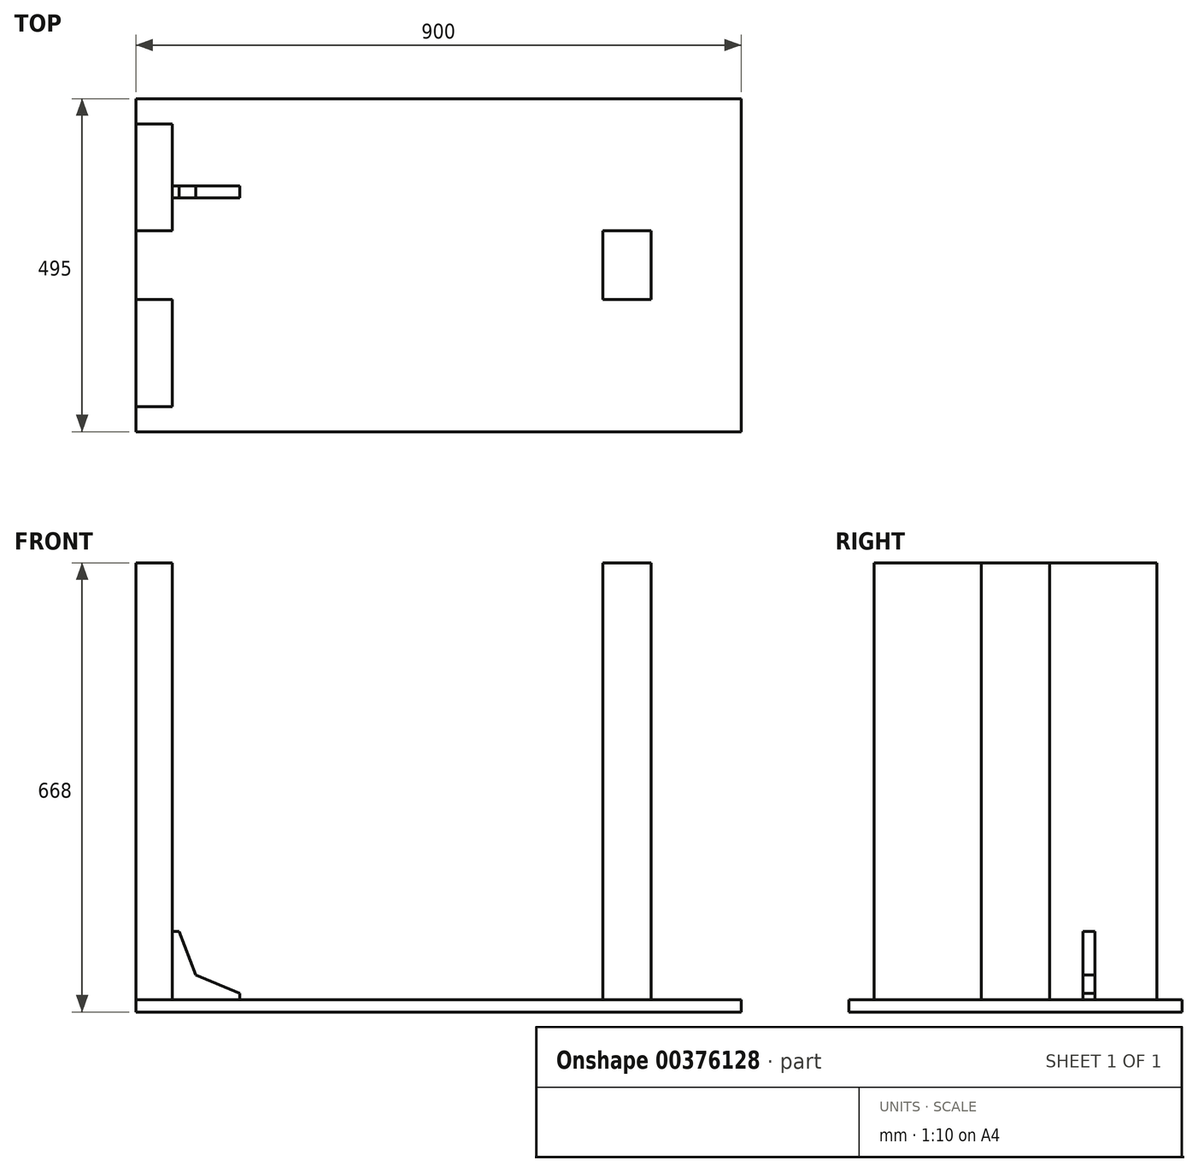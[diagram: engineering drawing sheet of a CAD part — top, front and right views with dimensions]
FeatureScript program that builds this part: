
annotation { "Feature Type Name" : "Feature", "Feature Type Description" : "" }
export const myFeature = defineFeature(function(context is Context, id is Id, definition is map)
    precondition{}
    {
        {
            var Q0;
            Q0=qCreatedBy(makeId("Top.planeOp"),FACE);
            var sketch = newSketch(context, id + "F0", { "sketchPlane" : qUnion([Q0])});
            skLineSegment(sketch, "E0.bottom", {"start": v(-450, 247.5) * mm, "end": v(450, 247.5) * mm});
            skLineSegment(sketch, "E0.top", {"start": v(-450, -247.5) * mm, "end": v(450, -247.5) * mm});
            skLineSegment(sketch, "E0.left", {"start": v(-450, 247.5) * mm, "end": v(-450, -247.5) * mm});
            skLineSegment(sketch, "E0.right", {"start": v(450, 247.5) * mm, "end": v(450, -247.5) * mm});
            skPoint(sketch, "E1", {"position": v(0, 247.5) * mm});
            skPoint(sketch, "E2", {"position": v(-450, 0) * mm});
            skSolve(sketch);
        }
        {
            var Q0;
            Q0=qSketchRegion(id+"F0",true);
            extrude(context, id + "F1", {"entities" : qUnion([Q0]), "depth" : 18 * mm});
        }
        {
            var Q0;
            Q0=makeQuery(id+"F1.opExtrude","CAP_FACE",FACE,{"disambiguationData":[OSD([sQuery(id+"F0.wireOp",EDGE,"E0.bottom"),sQuery(id+"F0.wireOp",EDGE,"E0.top"),sQuery(id+"F0.wireOp",EDGE,"E0.left"),sQuery(id+"F0.wireOp",EDGE,"E0.right")])],"isStart":false});
            var sketch = newSketch(context, id + "F2", { "sketchPlane" : qUnion([Q0])});
            skPoint(sketch, "E3", {"position": v(-450, 0) * mm});
            skLineSegment(sketch, "E4.bottom", {"start": v(-450, 210) * mm, "end": v(-396, 210) * mm});
            skLineSegment(sketch, "E4.top", {"start": v(-450, -210) * mm, "end": v(-396, -210) * mm});
            skLineSegment(sketch, "E4.left", {"start": v(-450, 210) * mm, "end": v(-450, -210) * mm});
            skLineSegment(sketch, "E4.right", {"start": v(-396, 210) * mm, "end": v(-396, -210) * mm});
            skLineSegment(sketch, "E5.bottom", {"start": v(316, -51) * mm, "end": v(244, -51) * mm});
            skLineSegment(sketch, "E5.top", {"start": v(316, 51) * mm, "end": v(244, 51) * mm});
            skLineSegment(sketch, "E5.left", {"start": v(316, -51) * mm, "end": v(316, 51) * mm});
            skLineSegment(sketch, "E5.right", {"start": v(244, -51) * mm, "end": v(244, 51) * mm});
            skPoint(sketch, "E6", {"position": v(316, 0) * mm});
            skPoint(sketch, "E7", {"position": v(0, -247.5) * mm});
            skSolve(sketch);
        }
        {
            var Q0;
            {var subQ1=sQuery(id+"F2.wireOp",EDGE,"E4.bottom");Q0=makeQuery(id+"F2.imprint","IMPRINT",FACE,{"disambiguationData":[TD([[makeQuery(id+"F2.imprint","IMPRINT",EDGE,{"derivedFrom":subQ1}),-1.0]])]});}
            var Q1;
            Q1=makeQuery(id+"F2.imprint","IMPRINT",FACE,{"disambiguationData":[TD([[makeQuery(id+"F2.imprint","IMPRINT",EDGE,{"derivedFrom":sQuery(id+"F2.wireOp",EDGE,"1kVaZgk3-8Nhi-dGg9-Ba8R-nr3TmBuge7lK.bottom")}),-1.0]])]});
            var Q2;
            Q2=makeQuery(id+"F2.imprint","IMPRINT",FACE,{"disambiguationData":[TD([[makeQuery(id+"F2.imprint","IMPRINT",EDGE,{"derivedFrom":sQuery(id+"F2.wireOp",EDGE,"d1aede41-c4be-4dbf-9319-fc5a6116a92b.bottom")}),-1.0]])]});
            var Q3;
            {var subQ1=sQuery(id+"F2.wireOp",EDGE,"E5.bottom");Q3=makeQuery(id+"F2.imprint","IMPRINT",FACE,{"disambiguationData":[TD([[makeQuery(id+"F2.imprint","IMPRINT",EDGE,{"derivedFrom":subQ1}),-1.0]])]});}
            extrude(context, id + "F3", {"entities" : qUnion([Q0, Q1, Q2, Q3]), "depth" : 650 * mm});
        }
        {
            var Q0;
            Q0=makeQuery(id+"F3.opExtrude","SWEPT_FACE",FACE,{"disambiguationData":[OSD([sQuery(id+"F2.wireOp",EDGE,"E5.left")])]});
            var sketch = newSketch(context, id + "F4", { "sketchPlane" : qUnion([Q0])});
            skLineSegment(sketch, "E8.bottom", {"start": v(51, 18) * mm, "end": v(-51, 18) * mm});
            skLineSegment(sketch, "E8.top", {"start": v(51, 668) * mm, "end": v(-51, 668) * mm});
            skLineSegment(sketch, "E8.left", {"start": v(51, 18) * mm, "end": v(51, 668) * mm});
            skLineSegment(sketch, "E8.right", {"start": v(-51, 18) * mm, "end": v(-51, 668) * mm});
            skPoint(sketch, "E9", {"position": v(0, 18) * mm});
            skPoint(sketch, "E10", {"position": v(140, 18) * mm});
            skPoint(sketch, "E11", {"position": v(-140, 18) * mm});
            skPoint(sketch, "E12", {"position": v(140, 668) * mm});
            skPoint(sketch, "E13", {"position": v(-140, 668) * mm});
            skLineSegment(sketch, "E14", {"start": v(51, 18) * mm, "end": v(140, 668) * mm});
            skLineSegment(sketch, "E15", {"start": v(-140, 668) * mm, "end": v(-51, 18) * mm});
            skSolve(sketch);
        }
        {
            var Q0;
            {var subQ0=sQuery(id+"F4.wireOp",EDGE,"E8.left");Q0=makeQuery(id+"F4.imprint","IMPRINT",FACE,{"disambiguationData":[TD([[makeQuery(id+"F4.imprint","IMPRINT",EDGE,{"derivedFrom":subQ0}),-1.0]])]});}
            var Q1;
            {var subQ0=sQuery(id+"F4.wireOp",EDGE,"E8.right");Q1=makeQuery(id+"F4.imprint","IMPRINT",FACE,{"disambiguationData":[TD([[makeQuery(id+"F4.imprint","IMPRINT",EDGE,{"derivedFrom":subQ0}),1.0]])]});}
            var Q2;
            {var subQ3=sQuery(id+"F4.wireOp",EDGE,"ERWEisdO-8PsZ-Fccj-wROh-Rmm69zbihmoK");Q2=makeQuery(id+"F4.imprint","IMPRINT",FACE,{"disambiguationData":[TD([[makeQuery(id+"F4.imprint","IMPRINT",EDGE,{"derivedFrom":subQ3}),-1.0]])]});}
            var Q3;
            {var subQ3=sQuery(id+"F4.wireOp",EDGE,"njEO2kw1-x9P7-cku3-6qRM-CGIWQrq0eT6F");Q3=makeQuery(id+"F4.imprint","IMPRINT",FACE,{"disambiguationData":[TD([[makeQuery(id+"F4.imprint","IMPRINT",EDGE,{"derivedFrom":subQ3}),1.0]])]});}
            var Q4;
            {var subQ0=sQuery(id+"F4.wireOp",EDGE,"ERWEisdO-8PsZ-Fccj-wROh-Rmm69zbihmoK");Q4=makeQuery(id+"F4.imprint","IMPRINT",FACE,{"disambiguationData":[TD([[makeQuery(id+"F4.imprint","IMPRINT",EDGE,{"derivedFrom":subQ0}),1.0]])]});}
            var Q5;
            {var subQ0=sQuery(id+"F4.wireOp",EDGE,"njEO2kw1-x9P7-cku3-6qRM-CGIWQrq0eT6F");Q5=makeQuery(id+"F4.imprint","IMPRINT",FACE,{"disambiguationData":[TD([[makeQuery(id+"F4.imprint","IMPRINT",EDGE,{"derivedFrom":subQ0}),-1.0]])]});}
            extrude(context, id + "F5", {"entities" : qUnion([Q0, Q1, Q2, Q3, Q4, Q5]), "operationType" : NewBodyOperationType.REMOVE, "endBound" : BoundingType.THROUGH_ALL, "oppositeDirection" : true, "depth" : 25 * mm});
        }
        {
            var Q0;
            Q0=makeQuery(id+"F3.opExtrude","SWEPT_FACE",FACE,{"disambiguationData":[OSD([sQuery(id+"F2.wireOp",EDGE,"E4.right"),sQuery(id+"F2.wireOp",EDGE,"1kVaZgk3-8Nhi-dGg9-Ba8R-nr3TmBuge7lK.left")])]});
            var sketch = newSketch(context, id + "F6", { "sketchPlane" : qUnion([Q0])});
            skLineSegment(sketch, "E16.bottom", {"start": v(118, 18) * mm, "end": v(100, 18) * mm});
            skLineSegment(sketch, "E16.top", {"start": v(118, 120) * mm, "end": v(100, 120) * mm});
            skLineSegment(sketch, "E16.left", {"start": v(118, 18) * mm, "end": v(118, 120) * mm});
            skLineSegment(sketch, "E16.right", {"start": v(100, 18) * mm, "end": v(100, 120) * mm});
            skSolve(sketch);
        }
        {
            var Q0;
            Q0=makeQuery(id+"F6.imprint","IMPRINT",FACE,{"disambiguationData":[TD([[makeQuery(id+"F6.imprint","IMPRINT",EDGE,{"derivedFrom":sQuery(id+"F6.wireOp",EDGE,"E16.bottom")}),-1.0]])]});
            extrude(context, id + "F7", {"entities" : qUnion([Q0]), "depth" : 100 * mm});
        }
        {
            var Q0;
            {var subQ1=sQuery(id+"F2.wireOp",EDGE,"E5.bottom");Q0=makeQuery(id+"F2.imprint","IMPRINT",FACE,{"disambiguationData":[TD([[makeQuery(id+"F2.imprint","IMPRINT",EDGE,{"derivedFrom":subQ1}),-1.0]])]});}
            extrude(context, id + "F8", {"entities" : qUnion([Q0]), "depth" : 650 * mm});
        }
        {
            var Q0;
            Q0=makeQuery(id+"F7.opExtrude","SWEPT_FACE",FACE,{"disambiguationData":[OSD([sQuery(id+"F6.wireOp",EDGE,"E16.left")])]});
            var sketch = newSketch(context, id + "F9", { "sketchPlane" : qUnion([Q0])});
            skLineSegment(sketch, "E17", {"start": v(411.5, 69.3) * mm, "end": v(366.5, 69.3) * mm});
            skLineSegment(sketch, "E18", {"start": v(424.53, 103.17) * mm, "end": v(379.53, 103.17) * mm});
            skLineSegment(sketch, "E19", {"start": v(351.8, 6.18) * mm, "end": v(351.8, 51.18) * mm});
            skLineSegment(sketch, "E20", {"start": v(311.36, 9.38) * mm, "end": v(311.36, 34.38) * mm});
            skLineSegment(sketch, "E21", {"start": v(386, 120) * mm, "end": v(361, 55) * mm});
            skLineSegment(sketch, "E22", {"start": v(361, 55) * mm, "end": v(296, 28) * mm});
            skLineSegment(sketch, "E23.bottom", {"start": v(396, 18) * mm, "end": v(296, 18) * mm});
            skLineSegment(sketch, "E23.top", {"start": v(396, 120) * mm, "end": v(296, 120) * mm});
            skLineSegment(sketch, "E23.left", {"start": v(396, 18) * mm, "end": v(396, 120) * mm});
            skLineSegment(sketch, "E23.right", {"start": v(296, 18) * mm, "end": v(296, 120) * mm});
            skSolve(sketch);
        }
        {
            var Q0;
            {var subQ2=sQuery(id+"F9.wireOp",EDGE,"E21");var subQ4=makeQuery(id+"F9.imprint","INTERSECT",VERTEX,{"derivedFrom":[sQuery(id+"F9.wireOp",EDGE,"E17"),subQ2]});Q0=makeQuery(id+"F9.imprint","IMPRINT",FACE,{"disambiguationData":[TD([[makeQuery(id+"F9.imprint","IMPRINT",EDGE,{"disambiguationData":[TD([[subQ4,1.0]])],"derivedFrom":subQ2}),-1.0]])]});}
            extrude(context, id + "F10", {"entities" : qUnion([Q0]), "operationType" : NewBodyOperationType.REMOVE, "oppositeDirection" : true, "depth" : 25 * mm});
        }
    });
